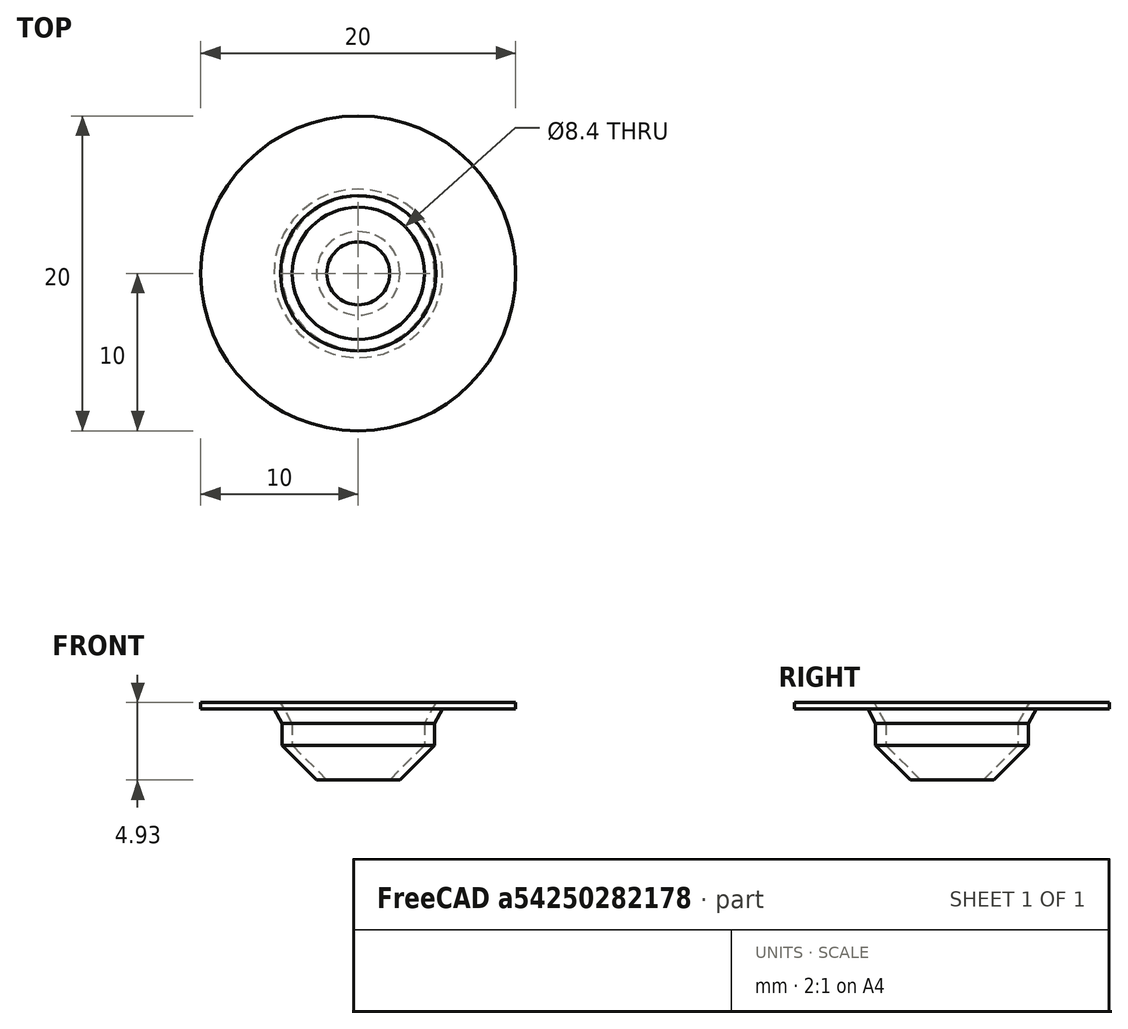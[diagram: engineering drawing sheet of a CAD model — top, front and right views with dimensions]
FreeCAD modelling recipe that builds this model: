
FCSTD DOCUMENT  (FreeCAD 0.15R4671 (Git))
Label: v3
License: CC-BY 3.0
LicenseURL: http://creativecommons.org/licenses/by/3.0/
objects: Sketcher::SketchObject×5, Mesh::Feature×1, PartDesign::Revolution×1
note: 7 computed .brp shape members not serialized (recipe doc carries the construction recipe); baked Part::Feature solids carry a one-line shape summary decoded from their .brp

FEATURE [Mesh::Feature] M2_Electrode_Mount_B_01  label="M2_Electrode Mount B_01"
FEATURE [Sketcher::SketchObject] Sketch
  sketch-geometry (2):
    g0: Circle CenterX=0 CenterY=0 CenterZ=0 NormalX=0 NormalY=0 NormalZ=1 Radius=5.35
    g1: Circle CenterX=0 CenterY=0 CenterZ=0 NormalX=0 NormalY=0 NormalZ=1 Radius=10
  constraints (2):
    c: Coincident(g0,g-1)
    c: Coincident(g1,g-1)
FEATURE [Sketcher::SketchObject] Sketch001
  Placement = pos=(0,0,-0.9) rot=(0,0,1;0rad)
  sketch-geometry (1):
    g0: Circle CenterX=0 CenterY=0 CenterZ=0 NormalX=0 NormalY=0 NormalZ=1 Radius=4.85008
  constraints (1):
    c: Coincident(g0,g-1)
FEATURE [Sketcher::SketchObject] Sketch002
  Placement = pos=(0,0,-2.3) rot=(0,0,1;0rad)
  sketch-geometry (1):
    g0: Circle CenterX=0 CenterY=0 CenterZ=0 NormalX=0 NormalY=0 NormalZ=1 Radius=4.85
  constraints (1):
    c: Coincident(g0,g-1)
FEATURE [Sketcher::SketchObject] Sketch004
  Placement = pos=(0,0,-4.5) rot=(0,0,1;0rad)
  sketch-geometry (2):
    g0: Circle CenterX=0 CenterY=0 CenterZ=0 NormalX=0 NormalY=0 NormalZ=1 Radius=2.65073
    g1: Circle CenterX=0 CenterY=0 CenterZ=0 NormalX=0 NormalY=0 NormalZ=1 Radius=2.00003
  constraints (2):
    c: Coincident(g0,g-1)
    c: Coincident(g1,g-1)
FEATURE [Sketcher::SketchObject] Sketch005
  Placement = pos=(0,0,0) rot=(-1,0,0;4.71239rad)
  sketch-geometry (10):
    g0: LineSegment StartX=2 StartY=-4.5 StartZ=0 EndX=2.65074 EndY=-4.5 EndZ=0
    g1: LineSegment StartX=2.65074 StartY=-4.5 StartZ=0 EndX=4.85006 EndY=-2.29993 EndZ=0
    g2: LineSegment StartX=4.85006 StartY=-2.29993 StartZ=0 EndX=4.85006 EndY=-0.900001 EndZ=0
    g3: LineSegment StartX=4.85006 StartY=-0.900001 StartZ=0 EndX=5.35009 EndY=0 EndZ=0
    g4: LineSegment StartX=5.35009 StartY=0 StartZ=0 EndX=10 EndY=0 EndZ=0
    g5: LineSegment StartX=10 StartY=0 StartZ=0 EndX=10 EndY=0.428388 EndZ=0
    g6: LineSegment StartX=10 StartY=0.428388 StartZ=0 EndX=4.93781 EndY=0.428388 EndZ=0
    g7: LineSegment StartX=4.93781 StartY=0.428388 StartZ=0 EndX=4.19944 EndY=-0.900596 EndZ=0
    g8: LineSegment StartX=4.19944 StartY=-0.900596 StartZ=0 EndX=4.19944 EndY=-2.29981 EndZ=0
    g9: LineSegment StartX=4.19944 StartY=-2.29981 StartZ=0 EndX=2 EndY=-4.5 EndZ=0
  constraints (28):
    c: Coincident(g0,g1)
    c: Coincident(g1,g2)
    c: Coincident(g2,g3)
    c: Coincident(g3,g4)
    c: Coincident(g4,g5)
    c: Coincident(g5,g6)
    c: Coincident(g6,g7)
    c: Coincident(g7,g8)
    c: Coincident(g8,g9)
    c: Coincident(g9,g0)
    c: Parallel(g6,g4)
    c: Parallel(g4,g0)
    c: Parallel(g5,g2)
    c: Parallel(g2,g8)
    c: Perpendicular(g0,g5)
    c: PointOnObject(g3,g-1)
    c: Parallel(g9,g1)
    c: Parallel(g7,g3)
    c: DistanceX(g0) = 2
    c: DistanceY(g0) = -4.5
    c: DistanceX(g4) = 10
    c: DistanceX(g0) = 2.65074
    c: DistanceY(g0) = -4.5
    c: DistanceX(g1) = 4.85006
    c: DistanceY(g1) = -2.29993
    c: DistanceY(g2) = -0.900001
    c: DistanceX(g3) = 5.35009
    c: DistanceX(g8) = 4.19944
FEATURE [PartDesign::Revolution] Revolution
  Angle = 360
  Axis = (0,0,1)
  Base = (0,0,0)
  Placement = pos=(0,0,0) rot=(-1,0,0;4.71239rad)
  ReferenceAxis = -> Sketch005 [V_Axis]
  Reversed = true
  Sketch = -> Sketch005
